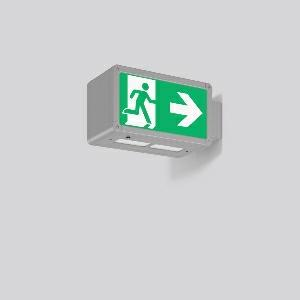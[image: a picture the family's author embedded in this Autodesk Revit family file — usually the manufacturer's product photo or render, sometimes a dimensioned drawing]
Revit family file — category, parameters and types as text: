
# Revit family: rechteck_wandausleger_671049_004_b12e
name_source: partatom
category: Lighting Fixtures
units: mm (PartAtom-declared; Revit-internal decimal feet)

## family parameters
Cut with Voids When Loaded = No
Host = Face
Light Source = No
Part Type = Normal
Room Calculation Point = No
Round Connector Dimension = Use Diameter
Shared = No

## types (1)
- RECHTECK wandausleger
    Apparent Load = 0 VA
    Default Elevation = 1800 mm
    Description = Series: RECHTECK
Rectangular wall extension luminaire in classic design. For escape route identification. Housing: aluminium, with plastic corner connectors. Display panels: plastic, opal, with motifs on one side/on both sides. Wall extension Electronic ballast included. Self-contained system with automatic self-test. Please indicate legend number when placing your order! 
Colour: anodised aluminium
Length: 250 mm
Width: 125 mm
Height: 140 mm
Weight: 1.6 kg
Operating mode: maintained power mode
Viewing Distance: 21 m
Duration time: 3 h
Lamp: LED
Socket: without socket
Colour temperature: 6500K
Colour rendering index (CRI): 70
System power: 6.9 W
Control gear: Regulated power supply
Protection class: I
Type of protection: IP 44
    Height = 140 mm  [stored 0.459318 ft]
    Lamp = 0 x
    Length = 250 mm
    Luminous efficacy = 0 lm/W
    Manufacturer = RZB
    ModVariant = No
    Model = 671049.004
    Mounting Place = Wall
    Mounting Type = Surface mounted
    Number of Poles = 1
    OnlyDefault = Yes
    Power Factor = 1
    Product Name = RECHTECK wandausleger
    Product group = wall cantilever luminaires
    ProductGroupID = 2005
    Protection Class = Protection class I
    Protection Degree = IP 44
    RLX_Detail_Level = 1
    RLX_Emergency_Light_Flux = 0 lm
    RLX_Emergency_Type = 0
    RLX_Emergency_Type_DB = No
    RlxData = <blob elided: 22617 chars, md5=4857b7f9>
    Standby Power = 0 W
    System Light Flux = 0 lm
    System Power = 0 W
    Type Comments = Product without accessories
    Type Image = 671049.004.jpg
    URL = http://relux.com
    VarID = ---
    Voltage = 230 V
    Voltage Range = 220-240 V
    Weight = 0.00 kg
    Width = 125 mm

note: [stored X ft] marks values corroborated as IEEE doubles in the binary element streams (Revit-internal decimal feet)

## geometry (parser evidence)
native form markers: Blend x4, Sweep x11
no freeform markers — native parametric forms only
